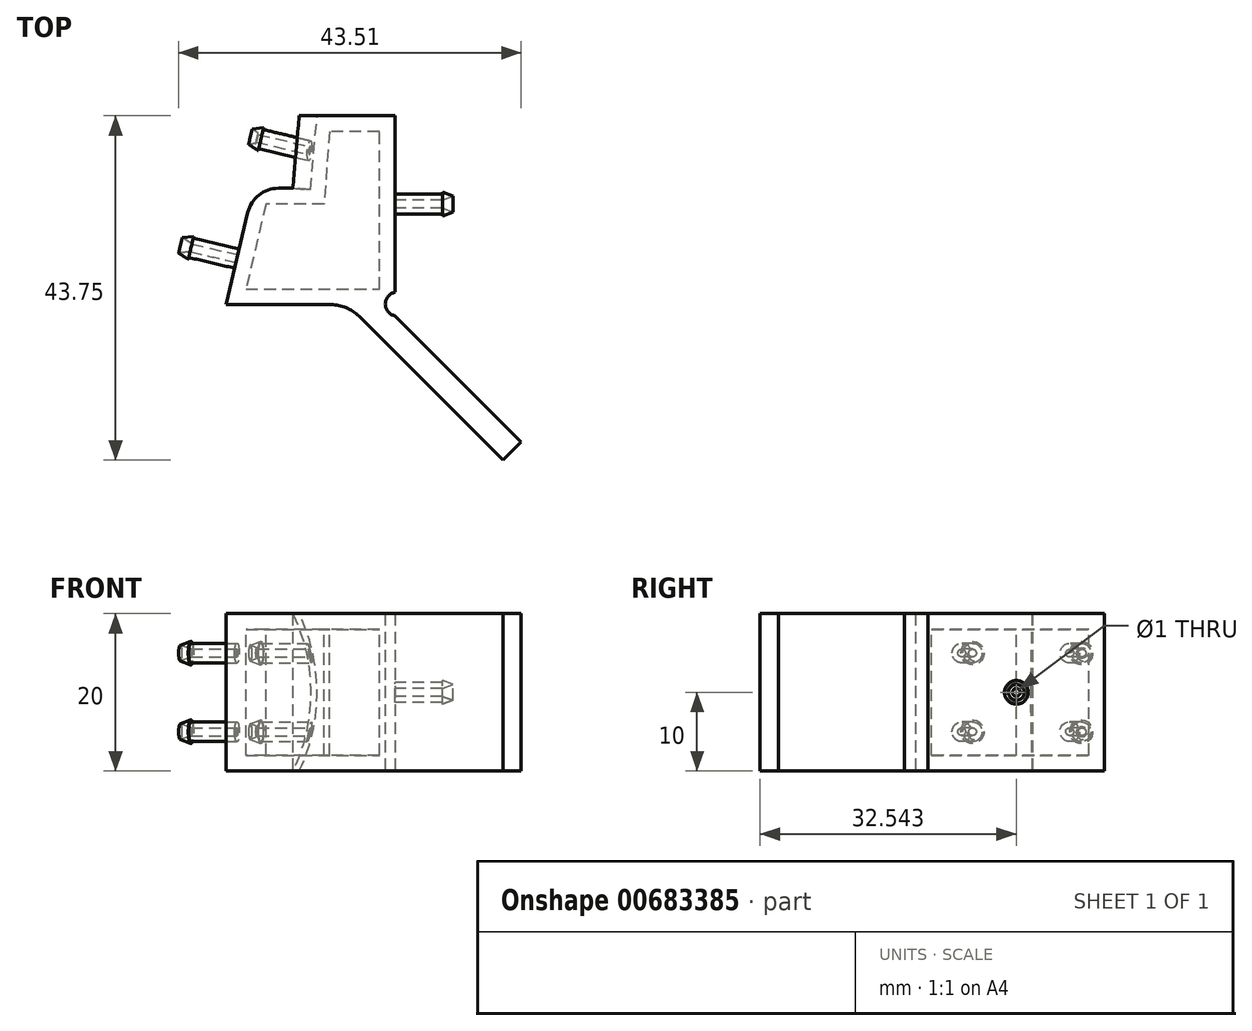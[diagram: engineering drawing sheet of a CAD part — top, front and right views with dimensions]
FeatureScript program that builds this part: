
annotation { "Feature Type Name" : "Feature", "Feature Type Description" : "" }
export const myFeature = defineFeature(function(context is Context, id is Id, definition is map)
    precondition{}
    {
        {
            var Q0;
            Q0=qCreatedBy(makeId("Top.planeOp"),FACE);
            var sketch = newSketch(context, id + "F0", { "sketchPlane" : qUnion([Q0])});
            skLineSegment(sketch, "E0", {"start": v(25.8, 2.59) * mm, "end": v(25.8, 25) * mm});
            skLineSegment(sketch, "E1", {"start": v(10.97, 15.8) * mm, "end": v(12.79, 15.8) * mm});
            skLineSegment(sketch, "E2", {"start": v(4.33, 1) * mm, "end": v(7.07, 12.71) * mm});
            skLineSegment(sketch, "E3", {"start": v(13.6, 25) * mm, "end": v(12.8, 15.8) * mm});
            skPoint(sketch, "E4.visualSharp", {"position": v(7.8, 15.8) * mm});
            skArc(sketch, "E4.filletArc", {"start": v(10.97, 15.8) * mm, "mid": v(8.48, 14.93) * mm, "end": v(7.07, 12.71) * mm});
            skPoint(sketch, "E5.visualSharp", {"position": v(12.8, 15.8) * mm});
            skArc(sketch, "E5.filletArc", {"start": v(12.79, 15.8) * mm, "mid": v(12.8, 15.8) * mm, "end": v(12.8, 15.8) * mm});
            skLineSegment(sketch, "E6.trimOffspring", {"start": v(25.8, -0.41) * mm, "end": v(41.8, -16.42) * mm});
            skLineSegment(sketch, "E7.0", {"start": v(21.19, -0.46) * mm, "end": v(39.47, -18.75) * mm});
            skLineSegment(sketch, "E8", {"start": v(39.47, -18.75) * mm, "end": v(41.8, -16.42) * mm});
            skArc(sketch, "E9", {"start": v(25.8, 2.59) * mm, "mid": v(24.55, 1.09) * mm, "end": v(25.8, -0.41) * mm});
            skPoint(sketch, "E10.end.orphan", {"position": v(22.5, 1) * mm});
            skPoint(sketch, "E10.start.orphan", {"position": v(22.5, -1.78) * mm});
            skLineSegment(sketch, "E11.0", {"start": v(25.8, 25) * mm, "end": v(13.6, 25) * mm});
            skLineSegment(sketch, "E12.trimOffspring", {"start": v(17.65, 1) * mm, "end": v(4.33, 1) * mm});
            skPoint(sketch, "E13.visualSharp", {"position": v(19.73, 1) * mm});
            skArc(sketch, "E13.filletArc", {"start": v(21.19, -0.46) * mm, "mid": v(19.57, 0.62) * mm, "end": v(17.65, 1) * mm});
            skSolve(sketch);
        }
        {
            var Q0;
            Q0=makeQuery(id+"F0.imprint","IMPRINT",FACE,{"disambiguationData":[TD([[makeQuery(id+"F0.imprint","IMPRINT",EDGE,{"derivedFrom":sQuery(id+"F0.wireOp",EDGE,"E0")}),1.0]])]});
            extrude(context, id + "F1", {"entities" : qUnion([Q0]), "depth" : 20 * mm, "offsetDistance" : 25 * mm});
        }
        {
            var Q0;
            Q0=makeQuery(id+"F1.opExtrude","SWEPT_FACE",FACE,{"disambiguationData":[OSD([sQuery(id+"F0.wireOp",EDGE,"E2")])]});
            cPlane(context, id + "F2", {"entities" : qUnion([Q0]), "cplaneType" : CPlaneType.OFFSET, "offset" : 0 * mm, "width" : 150 * mm, "height" : 150 * mm});
        }
        {
            var Q0;
            Q0=qCreatedBy(id+"F2.planeOp",FACE);
            var sketch = newSketch(context, id + "F3", { "sketchPlane" : qUnion([Q0])});
            skCircle(sketch, "E14", {"center": v(-7.98, 5) * mm, "radius": 0.5 * mm});
            skCircle(sketch, "E15", {"center": v(-7.98, 15) * mm, "radius": 0.5 * mm});
            skCircle(sketch, "E16", {"center": v(-7.98, 15) * mm, "radius": 1.25 * mm});
            skCircle(sketch, "E17", {"center": v(-7.98, 5) * mm, "radius": 1.25 * mm});
            skSolve(sketch);
        }
        {
            var Q0;
            Q0 = qSketchRegion(id + "F3", true);
            extrude(context, id + "F4", {"entities" : qUnion([Q0]), "operationType" : NewBodyOperationType.ADD, "depth" : 6 * mm, "offsetDistance" : 25 * mm});
        }
        {
            var Q0;
            {var subQ8=sQuery(id+"F0.wireOp",EDGE,"E4.filletArc");var subQ10=sQuery(id+"F0.wireOp",EDGE,"E2");Q0=makeQuery(id+"F4.boolean.opBoolean","SPLIT",FACE,{"disambiguationData":[TD([makeQuery(id+"F1.opExtrude","SWEPT_FACE",FACE,{"disambiguationData":[OSD([subQ8])]})])],"derivedFrom":makeQuery(id+"F1.opExtrude","SWEPT_FACE",FACE,{"disambiguationData":[OSD([subQ10])]})});}
            cPlane(context, id + "F5", {"entities" : qUnion([Q0]), "cplaneType" : CPlaneType.OFFSET, "offset" : 6 * mm, "width" : 150 * mm, "height" : 150 * mm});
        }
        {
            var Q0;
            Q0=qCreatedBy(id+"F5.planeOp",FACE);
            var sketch = newSketch(context, id + "F6", { "sketchPlane" : qUnion([Q0])});
            skCircle(sketch, "E18", {"center": v(-7.98, 5) * mm, "radius": 1.5 * mm});
            skCircle(sketch, "E19", {"center": v(-7.98, 15) * mm, "radius": 1.5 * mm});
            skCircle(sketch, "E20", {"center": v(-7.98, 5) * mm, "radius": 0.5 * mm});
            skCircle(sketch, "E21", {"center": v(-7.98, 15) * mm, "radius": 0.5 * mm});
            skSolve(sketch);
        }
        {
            var Q0;
            Q0=makeQuery(id+"F6.imprint","IMPRINT",FACE,{"disambiguationData":[TD([[makeQuery(id+"F6.imprint","IMPRINT",EDGE,{"derivedFrom":sQuery(id+"F6.wireOp",EDGE,"E18")}),1.0]])]});
            var Q1;
            Q1=makeQuery(id+"F6.imprint","IMPRINT",FACE,{"disambiguationData":[TD([[makeQuery(id+"F6.imprint","IMPRINT",EDGE,{"derivedFrom":sQuery(id+"F6.wireOp",EDGE,"E19")}),1.0]])]});
            extrude(context, id + "F7", {"entities" : qUnion([Q0, Q1]), "operationType" : NewBodyOperationType.ADD, "depth" : 2 * mm, "offsetDistance" : 25 * mm, "hasDraft" : true, "draftAngle" : 20 * degree, "draftPullDirection" : true});
        }
        {
            var Q0;
            Q0=makeQuery(id+"F1.opExtrude","SWEPT_EDGE",EDGE,{"disambiguationData":[OSD([sQuery(id+"F0.wireOp",EDGE,"E3"),sQuery(id+"F0.wireOp",EDGE,"E11.0")])]});
            var Q1;
            Q1=makeQuery(id+"F1.opExtrude","CAP_EDGE",EDGE,{"disambiguationData":[OSD([sQuery(id+"F0.wireOp",EDGE,"E3")])],"isStart":false});
            cPlane(context, id + "F8", {"entities" : qUnion([Q0, Q1]), "cplaneType" : CPlaneType.LINE_ANGLE, "offset" : 25 * mm, "angle" : 90 * degree, "width" : 150 * mm, "height" : 150 * mm});
        }
        {
            var Q0;
            Q0=qCreatedBy(id+"F8.planeOp",FACE);
            var sketch = newSketch(context, id + "F9", { "sketchPlane" : qUnion([Q0])});
            skLineSegment(sketch, "E22", {"start": v(-11.36, 0) * mm, "end": v(-11.36, 20) * mm});
            skArc(sketch, "E23", {"start": v(-11.36, 20) * mm, "mid": v(-13.62, 10) * mm, "end": v(-11.36, 0) * mm});
            skPoint(sketch, "E24.start.orphan", {"position": v(-11.36, 10) * mm});
            skSolve(sketch);
        }
        {
            var Q0;
            Q0=makeQuery(id+"F9.imprint","IMPRINT",FACE,{"disambiguationData":[TD([[makeQuery(id+"F9.imprint","IMPRINT",EDGE,{"derivedFrom":sQuery(id+"F9.wireOp",EDGE,"E22")}),1.0]])]});
            var Q1;
            Q1=sQuery(id+"F9.wireOp",EDGE,"E22");
            var Q2;
            Q2=sQuery(id+"F9.wireOp",EDGE,"E23");
            extrude(context, id + "F10", {"entities" : qUnion([Q0]), "operationType" : NewBodyOperationType.REMOVE, "surfaceEntities" : qUnion([Q1, Q2]), "oppositeDirection" : true, "depth" : 9.23 * mm, "offsetDistance" : 25 * mm, "hasSecondDirection" : true, "secondDirectionOppositeDirection" : false, "secondDirectionDepth" : 2 * mm});
        }
        {
            var Q0;
            {var subQ8=sQuery(id+"F0.wireOp",EDGE,"E4.filletArc");var subQ10=sQuery(id+"F0.wireOp",EDGE,"E2");Q0=makeQuery(id+"F4.boolean.opBoolean","SPLIT",FACE,{"disambiguationData":[TD([makeQuery(id+"F1.opExtrude","SWEPT_FACE",FACE,{"disambiguationData":[OSD([subQ8])]})])],"derivedFrom":makeQuery(id+"F1.opExtrude","SWEPT_FACE",FACE,{"disambiguationData":[OSD([subQ10])]})});}
            cPlane(context, id + "F11", {"entities" : qUnion([Q0]), "cplaneType" : CPlaneType.OFFSET, "offset" : 8 * mm, "oppositeDirection" : true, "width" : 150 * mm, "height" : 150 * mm});
        }
        {
            var Q0;
            Q0=qCreatedBy(id+"F11.planeOp",FACE);
            var sketch = newSketch(context, id + "F12", { "sketchPlane" : qUnion([Q0])});
            skCircle(sketch, "E25", {"center": v(-23.45, 5) * mm, "radius": 0.5 * mm});
            skCircle(sketch, "E26", {"center": v(-23.45, 15) * mm, "radius": 0.5 * mm});
            skCircle(sketch, "E27", {"center": v(-23.45, 5) * mm, "radius": 1.25 * mm});
            skCircle(sketch, "E28", {"center": v(-23.45, 15) * mm, "radius": 1.25 * mm});
            skSolve(sketch);
        }
        {
            var Q0;
            Q0 = qSketchRegion(id + "F12", true);
            extrude(context, id + "F13", {"entities" : qUnion([Q0]), "operationType" : NewBodyOperationType.ADD, "depth" : 9 * mm, "offsetDistance" : 25 * mm});
        }
        {
            var Q0;
            Q0=qCreatedBy(id+"F11.planeOp",FACE);
            cPlane(context, id + "F14", {"entities" : qUnion([Q0]), "cplaneType" : CPlaneType.OFFSET, "offset" : 8.5 * mm, "width" : 150 * mm, "height" : 150 * mm});
        }
        {
            var Q0;
            Q0=qCreatedBy(id+"F14.planeOp",FACE);
            var sketch = newSketch(context, id + "F15", { "sketchPlane" : qUnion([Q0])});
            skCircle(sketch, "E29", {"center": v(-23.45, 5) * mm, "radius": 1.5 * mm});
            skCircle(sketch, "E30", {"center": v(-23.45, 15) * mm, "radius": 1.5 * mm});
            skCircle(sketch, "E31", {"center": v(-23.45, 5) * mm, "radius": 0.5 * mm});
            skCircle(sketch, "E32", {"center": v(-23.45, 15) * mm, "radius": 0.5 * mm});
            skSolve(sketch);
        }
        {
            var Q0;
            Q0=makeQuery(id+"F15.imprint","IMPRINT",FACE,{"disambiguationData":[TD([[makeQuery(id+"F15.imprint","IMPRINT",EDGE,{"derivedFrom":sQuery(id+"F15.wireOp",EDGE,"E29")}),1.0]])]});
            var Q1;
            Q1=makeQuery(id+"F15.imprint","IMPRINT",FACE,{"disambiguationData":[TD([[makeQuery(id+"F15.imprint","IMPRINT",EDGE,{"derivedFrom":sQuery(id+"F15.wireOp",EDGE,"E30")}),1.0]])]});
            var Q2;
            Q2=sQuery(id+"F15.wireOp",EDGE,"E29");
            var Q3;
            Q3=sQuery(id+"F15.wireOp",EDGE,"E31");
            var Q4;
            Q4=sQuery(id+"F15.wireOp",EDGE,"E30");
            var Q5;
            Q5=sQuery(id+"F15.wireOp",EDGE,"E32");
            extrude(context, id + "F16", {"entities" : qUnion([Q0, Q1]), "operationType" : NewBodyOperationType.ADD, "surfaceEntities" : qUnion([Q2, Q3, Q4, Q5]), "depth" : 1.5 * mm, "offsetDistance" : 25 * mm, "hasDraft" : true, "draftAngle" : 20 * degree, "draftPullDirection" : true});
        }
        {
            var Q0;
            Q0=makeQuery(id+"F1.opExtrude","CAP_FACE",FACE,{"disambiguationData":[OSD([sQuery(id+"F0.wireOp",EDGE,"E0"),sQuery(id+"F0.wireOp",EDGE,"E1"),sQuery(id+"F0.wireOp",EDGE,"E2"),sQuery(id+"F0.wireOp",EDGE,"E3"),sQuery(id+"F0.wireOp",EDGE,"E4.filletArc"),sQuery(id+"F0.wireOp",EDGE,"E5.filletArc"),sQuery(id+"F0.wireOp",EDGE,"E6.trimOffspring"),sQuery(id+"F0.wireOp",EDGE,"E7.0"),sQuery(id+"F0.wireOp",EDGE,"E8"),sQuery(id+"F0.wireOp",EDGE,"E9"),sQuery(id+"F0.wireOp",EDGE,"E11.0"),sQuery(id+"F0.wireOp",EDGE,"E12.trimOffspring"),sQuery(id+"F0.wireOp",EDGE,"E13.filletArc")])],"isStart":false});
            cPlane(context, id + "F17", {"entities" : qUnion([Q0]), "cplaneType" : CPlaneType.OFFSET, "offset" : 2 * mm, "oppositeDirection" : true, "width" : 150 * mm, "height" : 150 * mm});
        }
        {
            var Q0;
            Q0=qCreatedBy(id+"F17.planeOp",FACE);
            var sketch = newSketch(context, id + "F18", { "sketchPlane" : qUnion([Q0])});
            skLineSegment(sketch, "E33.0", {"start": v(9.38, 13.8) * mm, "end": v(6.85, 3) * mm});
            skLineSegment(sketch, "E33.1", {"start": v(16.76, 13.8) * mm, "end": v(9.38, 13.8) * mm});
            skLineSegment(sketch, "E33.2", {"start": v(6.85, 3) * mm, "end": v(23.8, 3) * mm});
            skLineSegment(sketch, "E33.5", {"start": v(23.8, 3) * mm, "end": v(23.8, 23) * mm});
            skLineSegment(sketch, "E33.6", {"start": v(23.8, 23) * mm, "end": v(17.45, 23) * mm});
            skLineSegment(sketch, "E34", {"start": v(17.45, 23) * mm, "end": v(16.76, 13.8) * mm});
            skSolve(sketch);
        }
        {
            var Q0;
            Q0 = qSketchRegion(id + "F18", true);
            extrude(context, id + "F19", {"entities" : qUnion([Q0]), "operationType" : NewBodyOperationType.REMOVE, "oppositeDirection" : true, "depth" : 16 * mm, "offsetDistance" : 25 * mm});
        }
        {
            var Q0;
            Q0=makeQuery(id+"F1.opExtrude","SWEPT_FACE",FACE,{"disambiguationData":[OSD([sQuery(id+"F0.wireOp",EDGE,"E0")])]});
            cPlane(context, id + "F20", {"entities" : qUnion([Q0]), "cplaneType" : CPlaneType.OFFSET, "offset" : 0 * mm, "width" : 150 * mm, "height" : 150 * mm});
        }
        {
            var Q0;
            Q0=qCreatedBy(id+"F20.planeOp",FACE);
            var sketch = newSketch(context, id + "F21", { "sketchPlane" : qUnion([Q0])});
            skLineSegment(sketch, "E35", {"start": v(13.8, 20) * mm, "end": v(13.8, 0) * mm, "construction": true});
            skCircle(sketch, "E36", {"center": v(13.8, 10) * mm, "radius": 0.5 * mm});
            skCircle(sketch, "E37", {"center": v(13.8, 10) * mm, "radius": 1.25 * mm});
            skSolve(sketch);
        }
        {
            var Q0;
            Q0=makeQuery(id+"F21.imprint","IMPRINT",FACE,{"disambiguationData":[TD([[makeQuery(id+"F21.imprint","IMPRINT",EDGE,{"derivedFrom":sQuery(id+"F21.wireOp",EDGE,"E36")}),-1.0]])]});
            var Q1;
            Q1=sQuery(id+"F21.wireOp",EDGE,"E35");
            var Q2;
            Q2=sQuery(id+"F21.wireOp",EDGE,"E37");
            var Q3;
            Q3=sQuery(id+"F21.wireOp",EDGE,"E36");
            extrude(context, id + "F22", {"entities" : qUnion([Q0]), "surfaceEntities" : qUnion([Q1, Q2, Q3]), "depth" : 6 * mm, "offsetDistance" : 25 * mm});
        }
        {
            var Q0;
            Q0=makeQuery(id+"F22.opExtrude","CAP_FACE",FACE,{"disambiguationData":[OSD([sQuery(id+"F21.wireOp",EDGE,"E36"),sQuery(id+"F21.wireOp",EDGE,"E37")])],"isStart":false});
            cPlane(context, id + "F23", {"entities" : qUnion([Q0]), "cplaneType" : CPlaneType.OFFSET, "offset" : 0 * mm, "width" : 150 * mm, "height" : 150 * mm});
        }
        {
            var Q0;
            Q0=qCreatedBy(id+"F23.planeOp",FACE);
            var sketch = newSketch(context, id + "F24", { "sketchPlane" : qUnion([Q0])});
            skCircle(sketch, "E38", {"center": v(13.8, 10) * mm, "radius": 0.5 * mm});
            skCircle(sketch, "E39", {"center": v(13.8, 10) * mm, "radius": 1.5 * mm});
            skSolve(sketch);
        }
        {
            var Q0;
            Q0 = qSketchRegion(id + "F24", true);
            extrude(context, id + "F25", {"entities" : qUnion([Q0]), "operationType" : NewBodyOperationType.ADD, "depth" : 3 * mm, "offsetDistance" : 25 * mm, "hasDraft" : true, "draftAngle" : 20 * degree, "draftPullDirection" : true});
        }
    });
